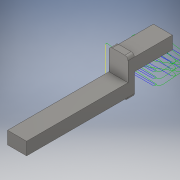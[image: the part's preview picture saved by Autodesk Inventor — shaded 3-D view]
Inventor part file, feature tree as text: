
AUTODESK INVENTOR PART (.ipt)
format: ipt  version: 2018 (Build 220112000, 112)  size: 220,160 bytes
history: native  units: in
note: dims shown in document units (in); Inventor stores cm internally (conversion verified against a paired STEP export)
features: extrude x5, sketch x5, fillet x1
ambient origin geometry x8: Origin, YZ Plane, XZ Plane, XY Plane, X Axis, Y Axis, Z Axis, Center Point
bodies: Solid1 (feature_tree)
feature tree (11):
  extrude  "Extrusion1"  Depth=2.875in
  extrude  "Extrusion2"  Depth=2.0in
  extrude  "Extrusion3"  Depth=0.375in TaperAngle=0.0deg
  extrude  "Extrusion4"  Depth=0.3125in
  extrude  "Extrusion5"  Depth=2.0in
  fillet  "Fillet1"  Radius=0.0625in
  sketch  "Sketch1"  dims[d0=0.75in d1=2.875in]
  sketch  "Sketch2"  dims[d2=0.375in d3=0.0in d4=2.0in]
  sketch  "Sketch3"  dims[d6=0.3125in d7=0.375in d8=0.0in]
  sketch  "Sketch4"  dims[d9=0.125in d10=0.3125in]
  sketch  "Sketch5"  dims[d11=0.375in d12=0.0in d13=2.0in d14=0.0625in d15=0.375in d16=0.0in d17=0.75in d18=0.0625in d19=0.375in d20=0.0in d31=0.0625in]
